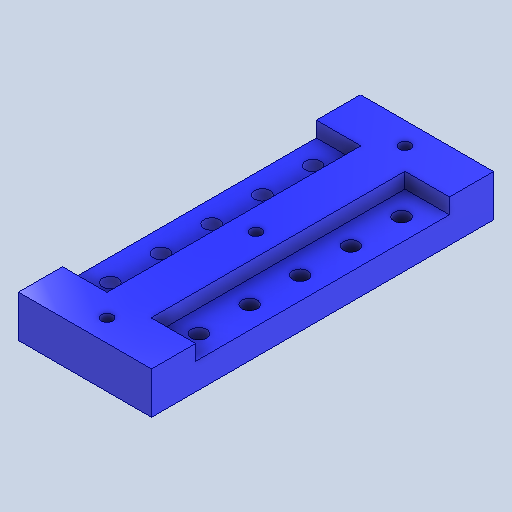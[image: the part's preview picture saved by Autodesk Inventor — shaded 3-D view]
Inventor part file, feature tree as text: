
AUTODESK INVENTOR PART (.ipt)
format: ipt  version: 2023 (Build 270158000, 158)  size: 214,528 bytes
history: native  units: in
note: dims shown in document units (in); Inventor stores cm internally (conversion verified against a paired STEP export)
features: extrude x3, sketch x2, plane x1, mirror x1, projected_geometry x1
ambient origin geometry x8: Origin, YZ Plane, XZ Plane, XY Plane, X Axis, Y Axis, Z Axis, Center Point
bodies: Solid1 (feature_tree)
feature tree (8):
  sketch  "Sketch1"  dims[d0=4.5354in d1=0.7953in]
  extrude  "Extrusion1"  Depth=0.7953in
  extrude  "Extrusion2"  Depth=0.7874in
  extrude  "Extrusion3"  Depth=0.7874in
  sketch  "Sketch2"  dims[d2=0.2756in d3=0.9055in d4=0.9055in d5=0.4724in d6=0.0in d7=0.0787in d8=0.0in d9=0.748in d10=0.0in d11=0.7874in d12=0.7874in d13=0.7874in d14=0.2047in d15=90.0deg]
  plane  "Work Plane1"
  mirror  "Mirror1"
  projected_geometry  "Projected Loop1"
